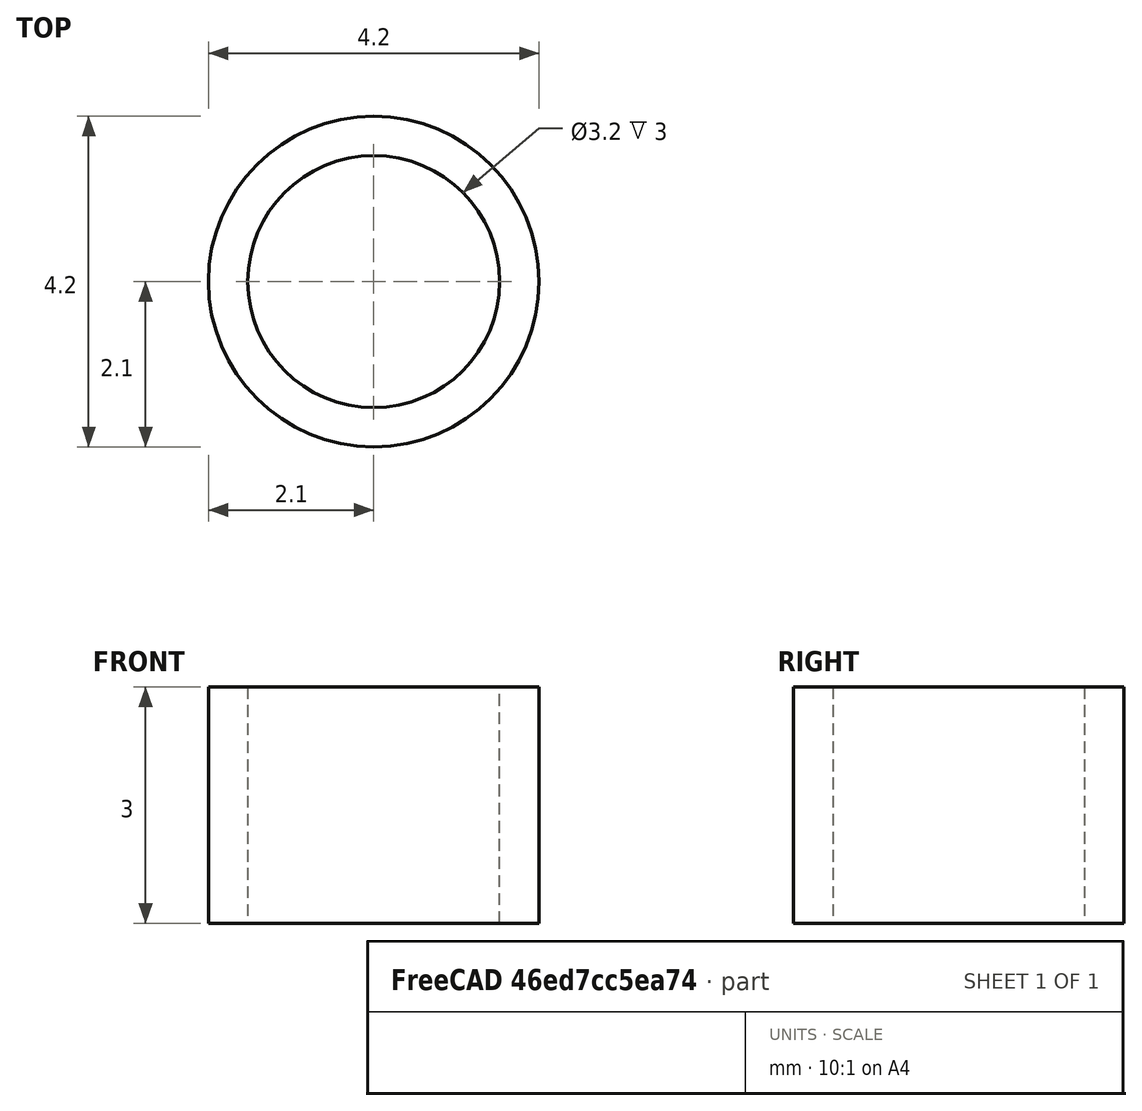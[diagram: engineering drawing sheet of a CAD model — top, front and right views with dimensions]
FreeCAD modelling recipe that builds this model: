
FCSTD DOCUMENT  (FreeCAD 2023.131R26244 +5365 (Git))
Label: shock-spacers
License: All rights reserved
LicenseURL: http://en.wikipedia.org/wiki/All_rights_reserved
objects: Sketcher::SketchObject×1, PartDesign::Pad×1, PartDesign::Body×1
note: 6 computed .brp shape members not serialized (recipe doc carries the construction recipe); baked Part::Feature solids carry a one-line shape summary decoded from their .brp

FEATURE [Sketcher::SketchObject] Sketch
  ArcFitTolerance = 1e-06
  AttachmentSupport = -> [XY_Plane]
  ExternalBSplineMaxDegree = 5
  ExternalBSplineTolerance = 0.0001
  FixShape = 1
  FullyConstrained = true
  InternalTolerance = 1e-06
  InvalidShape = false
  MakeInternals = false
  MapMode = 5
  Support = -> [XY_Plane]
  TreeRank = 11
  ValidateShape = false
  sketch-geometry (2):
    g0: Circle CenterX=0 CenterY=0 CenterZ=0 NormalX=0 NormalY=0 NormalZ=1 AngleXU=0 Radius=1.6
    g1: Circle CenterX=0 CenterY=0 CenterZ=0 NormalX=0 NormalY=0 NormalZ=1 AngleXU=0 Radius=2.1
  constraints (4):
    c: Coincident(g0,g-1)
    c: Coincident(g1,g0)
    c: Diameter(g0) = 3.2
    c: Diameter(g1) = 4.2
FEATURE [PartDesign::Pad] Pad
  AddSubType = 0
  AlongSketchNormal = false
  AutoTaperInnerAngle = true
  CheckUpToFaceLimits = true
  ClaimChildren = false
  Direction = (0,0,1)
  Fit = 0
  FitJoin = 0
  FixShape = 1
  InnerFit = 0
  InnerFitJoin = 0
  InvalidShape = false
  Length = 3
  Length2 = 100
  Linearize = true
  NewSolid = false
  Profile = -> Sketch
  Refine = true
  Suppress = false
  TaperInnerAngle = 0
  TaperInnerAngleRev = 0
  TreeRank = 12
  Type = 0
  ValidateShape = false
  _ProfileBasedVersion = 1
FEATURE [PartDesign::Body] Body  label="spacer"
  AutoGroupSolids = false
  ClaimAllChildren = false
  ExportMode = 0
  FixShape = 1
  Group = -> [Sketch,Pad]
  InvalidShape = false
  Origin = -> Origin
  Tip = -> Pad
  TreeRank = 10
  ValidateShape = false
  _ExportChildren = -> [Pad]
  _GroupVersion = 1
